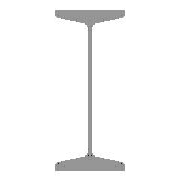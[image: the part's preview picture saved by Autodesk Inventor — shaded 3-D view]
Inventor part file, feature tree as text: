
AUTODESK INVENTOR PART (.ipt)
format: ipt  version: 2025 (Build 290162010, 162A)  size: 166,400 bytes
history: native  units: mm (DEFAULTED — no unit token found)
features: other x3, sketch x1, plane x1
ambient origin geometry x8: Origin, YZ Plane, XZ Plane, XY Plane, X Axis, Y Axis, Z Axis, Center Point
bodies: Solid1 (feature_tree), Body (feature_tree)
feature tree (5):
  other  "Driven Length"
  other  "Start plane"
  other  "End plane"
  sketch  "Sketch3"  dims[d1=3.94217mm d2=12.0mm d3=28.05mm d4=3.9mm d5=60.0mm d6=6000.0mm d7=0.0mm d10=120.0mm d14=6.0mm d15=12.0mm d16=-0.0mm d17=6000.0mm d18=90.0deg d19=6000.0mm]
  plane  "Work Plane3"
